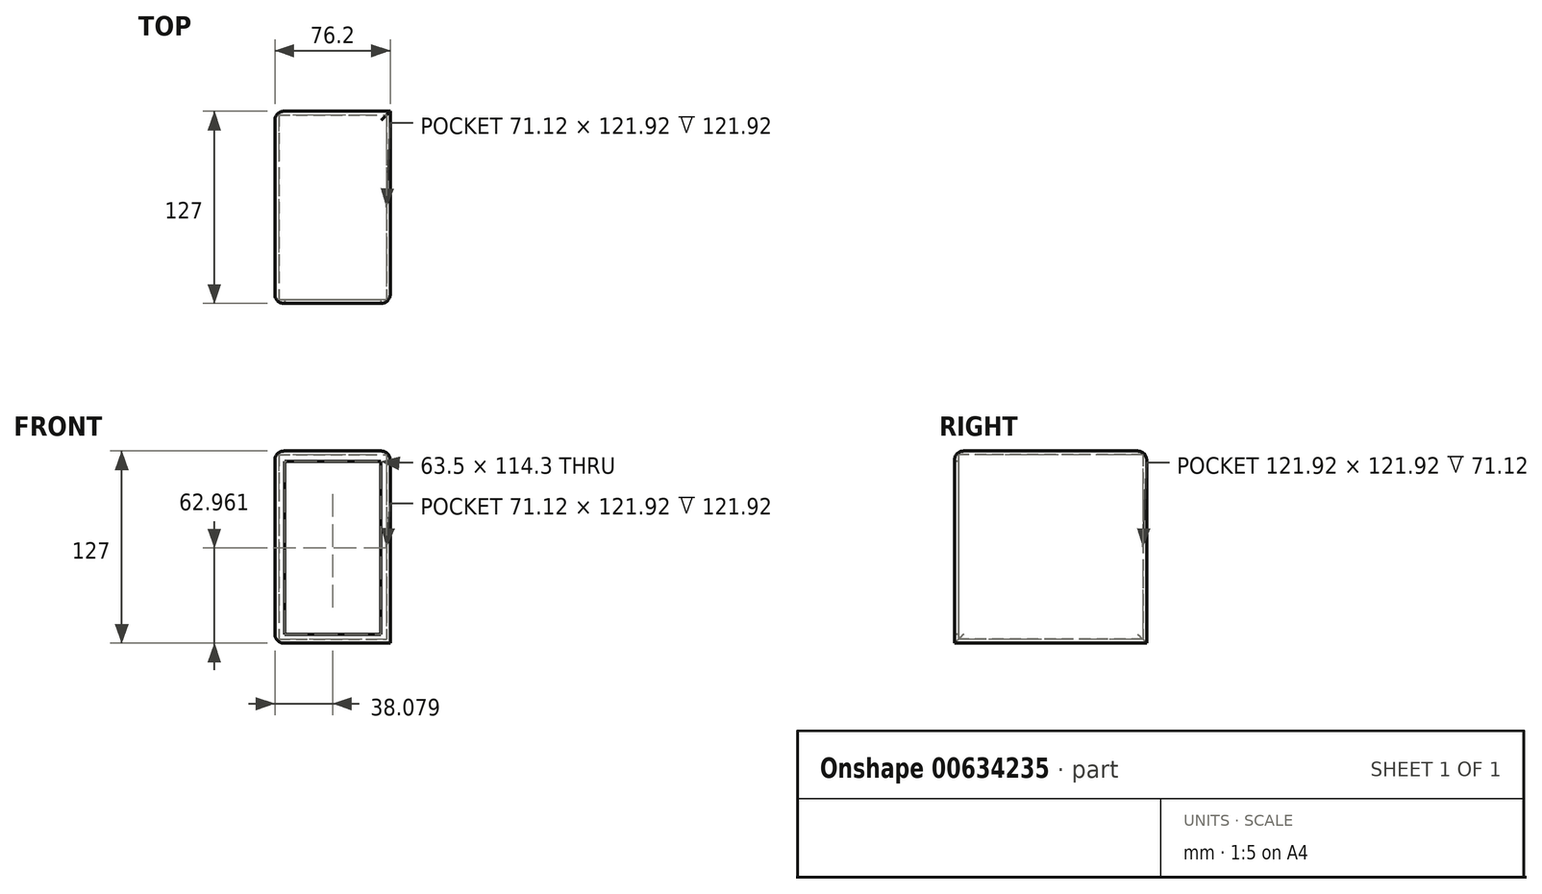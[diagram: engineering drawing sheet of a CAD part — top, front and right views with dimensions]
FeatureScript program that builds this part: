
annotation { "Feature Type Name" : "Feature", "Feature Type Description" : "" }
export const myFeature = defineFeature(function(context is Context, id is Id, definition is map)
    precondition{}
    {
        {
            var Q0;
            Q0=qCreatedBy(makeId("Front.planeOp"),FACE);
            var sketch = newSketch(context, id + "F0", { "sketchPlane" : qUnion([Q0])});
            skLineSegment(sketch, "E0.bottom", {"start": v(-76.2, 60.8) * mm, "end": v(0, 60.8) * mm});
            skLineSegment(sketch, "E0.top", {"start": v(-76.2, -66.2) * mm, "end": v(0, -66.2) * mm});
            skLineSegment(sketch, "E0.left", {"start": v(-76.2, 60.8) * mm, "end": v(-76.2, -66.2) * mm});
            skLineSegment(sketch, "E0.right", {"start": v(0, 60.8) * mm, "end": v(0, -66.2) * mm});
            skSolve(sketch);
        }
        {
            var Q0;
            Q0 = qSketchRegion(id + "F0", true);
            extrude(context, id + "F1", {"entities" : qUnion([Q0]), "oppositeDirection" : true, "depth" : 127 * mm, "offsetDistance" : 25.4 * mm});
        }
        {
            var Q0;
            Q0=makeQuery(id+"F1.opExtrude","CAP_FACE",FACE,{"disambiguationData":[OSD([sQuery(id+"F0.wireOp",EDGE,"E0.bottom"),sQuery(id+"F0.wireOp",EDGE,"E0.top"),sQuery(id+"F0.wireOp",EDGE,"E0.left"),sQuery(id+"F0.wireOp",EDGE,"E0.right")])],"isStart":true});
            var Q1;
            Q1=makeQuery(id+"F1.opExtrude","SWEPT_BODY",BODY,{"disambiguationData":[OSD([sQuery(id+"F0.wireOp",EDGE,"E0.bottom"),sQuery(id+"F0.wireOp",EDGE,"E0.top"),sQuery(id+"F0.wireOp",EDGE,"E0.left"),sQuery(id+"F0.wireOp",EDGE,"E0.right")])]});
            shell(context, id + "F2", {"isHollow" : true, "entities" : qUnion([Q0]), "parts" : qUnion([Q1]), "thickness" : 2.54 * mm});
        }
        {
            var Q0;
            Q0=makeQuery(id+"F1.opExtrude","CAP_FACE",FACE,{"disambiguationData":[OSD([sQuery(id+"F0.wireOp",EDGE,"E0.bottom"),sQuery(id+"F0.wireOp",EDGE,"E0.top"),sQuery(id+"F0.wireOp",EDGE,"E0.left"),sQuery(id+"F0.wireOp",EDGE,"E0.right")])],"isStart":true});
            var sketch = newSketch(context, id + "F3", { "sketchPlane" : qUnion([Q0])});
            skLineSegment(sketch, "E1.bottom", {"start": v(-69.87, 53.91) * mm, "end": v(-6.37, 53.91) * mm});
            skLineSegment(sketch, "E1.top", {"start": v(-69.87, -60.39) * mm, "end": v(-6.37, -60.39) * mm});
            skLineSegment(sketch, "E1.left", {"start": v(-69.87, 53.91) * mm, "end": v(-69.87, -60.39) * mm});
            skLineSegment(sketch, "E1.right", {"start": v(-6.37, 53.91) * mm, "end": v(-6.37, -60.39) * mm});
            skSolve(sketch);
        }
        {
            var Q0;
            Q0 = qSketchRegion(id + "F3", true);
            extrude(context, id + "F4", {"entities" : qUnion([Q0]), "operationType" : NewBodyOperationType.REMOVE, "oppositeDirection" : true, "depth" : 76.2 * mm, "offsetDistance" : 25.4 * mm});
        }
        {
            var Q0;
            Q0=makeQuery(id+"F1.opExtrude","SWEPT_EDGE",EDGE,{"disambiguationData":[OSD([sQuery(id+"F0.wireOp",EDGE,"E0.bottom"),sQuery(id+"F0.wireOp",EDGE,"E0.right")])]});
            var Q1;
            Q1=makeQuery(id+"F1.opExtrude","CAP_EDGE",EDGE,{"disambiguationData":[OSD([sQuery(id+"F0.wireOp",EDGE,"E0.bottom")])],"isStart":true});
            var Q2;
            Q2=makeQuery(id+"F1.opExtrude","CAP_EDGE",EDGE,{"disambiguationData":[OSD([sQuery(id+"F0.wireOp",EDGE,"E0.right")])],"isStart":true});
            var Q3;
            Q3=makeQuery(id+"F1.opExtrude","SWEPT_FACE",FACE,{"disambiguationData":[OSD([sQuery(id+"F0.wireOp",EDGE,"E0.left")])]});
            var Q4;
            Q4=makeQuery(id+"F1.opExtrude","CAP_EDGE",EDGE,{"disambiguationData":[OSD([sQuery(id+"F0.wireOp",EDGE,"E0.bottom")])],"isStart":false});
            fillet(context, id + "F5", {"entities" : qUnion([Q0, Q1, Q2, Q3, Q4]), "radius" : 6 * mm, "tangentPropagation" : true, "allowEdgeOverflow" : false});
        }
    });
